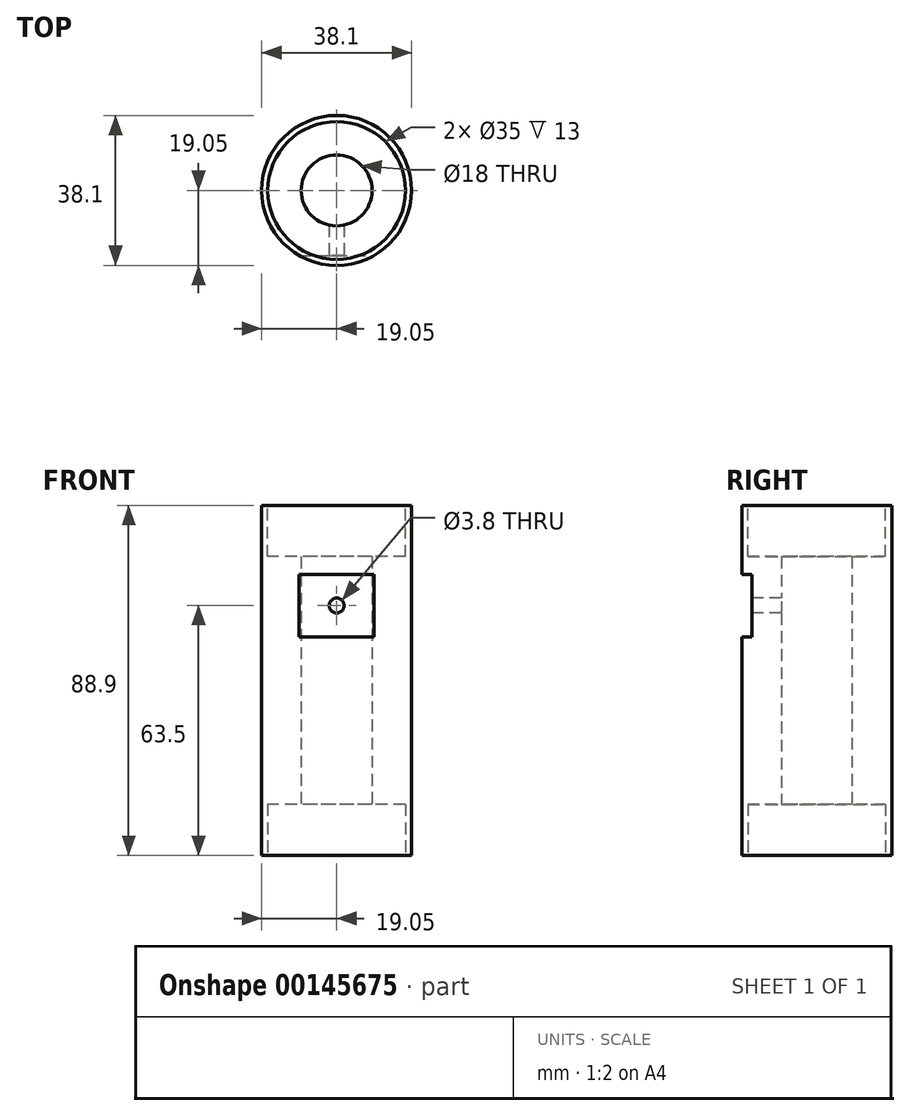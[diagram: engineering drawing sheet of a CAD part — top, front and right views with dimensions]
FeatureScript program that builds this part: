
annotation { "Feature Type Name" : "Feature", "Feature Type Description" : "" }
export const myFeature = defineFeature(function(context is Context, id is Id, definition is map)
    precondition{}
    {
        {
            var Q0;
            Q0=qCreatedBy(makeId("Top.planeOp"),FACE);
            var sketch = newSketch(context, id + "F0", { "sketchPlane" : qUnion([Q0])});
            skCircle(sketch, "E0", {"center": v(0, 0) * mm, "radius": 19.05 * mm});
            skCircle(sketch, "E1", {"center": v(0, 0) * mm, "radius": 9 * mm});
            skCircle(sketch, "E2", {"center": v(0, 0) * mm, "radius": 17.5 * mm});
            skSolve(sketch);
        }
        {
            var Q0;
            Q0=makeQuery(id+"F0.imprint","IMPRINT",FACE,{"disambiguationData":[TD([[makeQuery(id+"F0.imprint","IMPRINT",EDGE,{"derivedFrom":sQuery(id+"F0.wireOp",EDGE,"E0")}),1.0]])]});
            var Q1;
            Q1=makeQuery(id+"F0.imprint","IMPRINT",FACE,{"disambiguationData":[TD([[makeQuery(id+"F0.imprint","IMPRINT",EDGE,{"derivedFrom":sQuery(id+"F0.wireOp",EDGE,"E1")}),-1.0]])]});
            extrude(context, id + "F1", {"entities" : qUnion([Q0, Q1]), "depth" : 88.9 * mm});
        }
        {
            var Q0;
            Q0=makeQuery(id+"F0.imprint","IMPRINT",FACE,{"disambiguationData":[TD([[makeQuery(id+"F0.imprint","IMPRINT",EDGE,{"derivedFrom":sQuery(id+"F0.wireOp",EDGE,"E1")}),-1.0]])]});
            extrude(context, id + "F2", {"entities" : qUnion([Q0]), "operationType" : NewBodyOperationType.REMOVE, "depth" : 13 * mm});
        }
        {
            var Q0;
            Q0=makeQuery(id+"F1.opExtrude","CAP_FACE",FACE,{"disambiguationData":[OSD([sQuery(id+"F0.wireOp",EDGE,"E0"),sQuery(id+"F0.wireOp",EDGE,"E1")])],"isStart":false});
            var sketch = newSketch(context, id + "F3", { "sketchPlane" : qUnion([Q0])});
            skCircle(sketch, "E3.0", {"center": v(0, 0) * mm, "radius": 17.5 * mm});
            skSolve(sketch);
        }
        {
            var Q0;
            Q0=makeQuery(id+"F3.imprint","IMPRINT",FACE,{"disambiguationData":[TD([[makeQuery(id+"F3.imprint","IMPRINT",EDGE,{"derivedFrom":sQuery(id+"F3.wireOp",EDGE,"E3.0")}),1.0]])]});
            extrude(context, id + "F4", {"entities" : qUnion([Q0]), "operationType" : NewBodyOperationType.REMOVE, "oppositeDirection" : true, "depth" : 13 * mm});
        }
        {
            var Q0;
            Q0=qCreatedBy(makeId("Front.planeOp"),FACE);
            cPlane(context, id + "F5", {"entities" : qUnion([Q0]), "cplaneType" : CPlaneType.OFFSET, "offset" : 19.05 * mm, "width" : 152.4 * mm, "height" : 152.4 * mm});
        }
        {
            var Q0;
            Q0=qCreatedBy(id+"F5.planeOp",FACE);
            var sketch = newSketch(context, id + "F6", { "sketchPlane" : qUnion([Q0])});
            skLineSegment(sketch, "E4.bottom", {"start": v(-9.53, 71.44) * mm, "end": v(9.53, 71.44) * mm});
            skLineSegment(sketch, "E4.top", {"start": v(-9.53, 55.56) * mm, "end": v(9.53, 55.56) * mm});
            skLineSegment(sketch, "E4.left", {"start": v(-9.53, 71.44) * mm, "end": v(-9.53, 55.56) * mm});
            skLineSegment(sketch, "E4.right", {"start": v(9.52, 71.44) * mm, "end": v(9.52, 55.56) * mm});
            skPoint(sketch, "E5", {"position": v(0, 63.5) * mm});
            skLineSegment(sketch, "E6", {"start": v(0, 71.44) * mm, "end": v(0, 55.56) * mm, "construction": true});
            skSolve(sketch);
        }
        {
            var Q0;
            Q0=makeQuery(id+"F6.imprint","IMPRINT",FACE,{"disambiguationData":[TD([[makeQuery(id+"F6.imprint","IMPRINT",EDGE,{"derivedFrom":sQuery(id+"F6.wireOp",EDGE,"E4.bottom")}),-1.0]])]});
            extrude(context, id + "F7", {"entities" : qUnion([Q0]), "operationType" : NewBodyOperationType.REMOVE, "oppositeDirection" : true, "depth" : 2.54 * mm});
        }
        {
            var Q0;
            Q0=sQuery(id+"F6.wireOp",VERTEX,"E5");
            var Q1;
            Q1=makeQuery(id+"F1.opExtrude","SWEPT_BODY",BODY,{"disambiguationData":[OSD([sQuery(id+"F0.wireOp",EDGE,"E0"),sQuery(id+"F0.wireOp",EDGE,"E1")])]});
            hole(context, id + "F8", {"style" : HoleStyle.SIMPLE, "endStyle" : HoleEndStyle.BLIND, "standardTappedOrClearance" : lookupTablePath({ "standard" : "ANSI", "engagement" : "75%", "pitch" : "24 tpi", "size" : "#10", "type" : "Tapped" }), "standardBlindInLast" : lookupTablePath({ "standard" : "ANSI", "engagement" : "75%", "pitch" : "24 tpi", "size" : "#10", "type" : "Tapped" }), "holeDiameter" : 3.8 * mm, "holeDepth" : 12.7 * mm, "locations" : qUnion([Q0]), "scope" : qUnion([Q1]), "majorDiameter" : 4.83 * mm});
        }
    });
